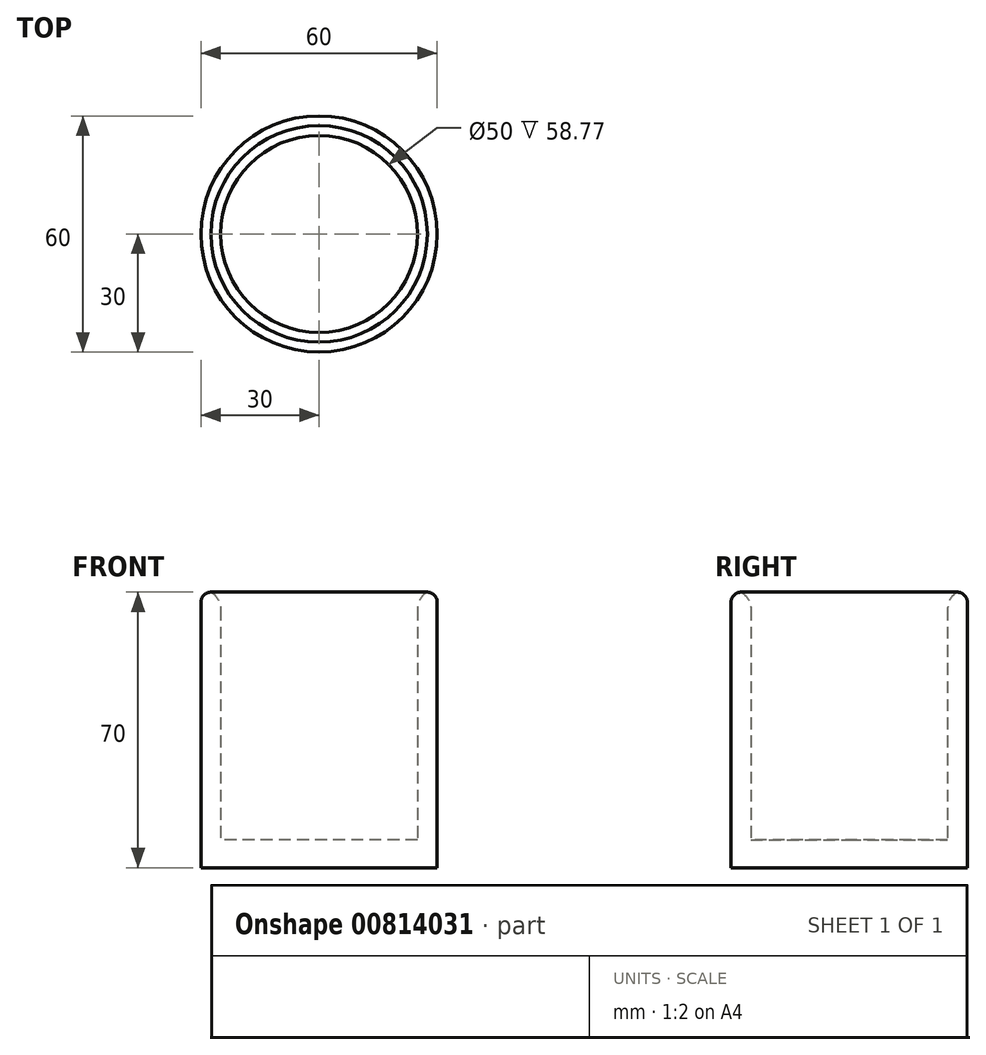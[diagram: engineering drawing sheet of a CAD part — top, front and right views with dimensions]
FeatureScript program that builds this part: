
annotation { "Feature Type Name" : "Feature", "Feature Type Description" : "" }
export const myFeature = defineFeature(function(context is Context, id is Id, definition is map)
    precondition{}
    {
        {
            var Q0;
            Q0=qCreatedBy(makeId("Top.planeOp"),FACE);
            var sketch = newSketch(context, id + "F0", { "sketchPlane" : qUnion([Q0])});
            skCircle(sketch, "E0", {"center": v(0, 0) * mm, "radius": 30 * mm});
            skCircle(sketch, "E1", {"center": v(0, 0) * mm, "radius": 25 * mm});
            skSolve(sketch);
        }
        {
            var Q0;
            Q0=makeQuery(id+"F0.imprint","IMPRINT",FACE,{"disambiguationData":[TD([[makeQuery(id+"F0.imprint","IMPRINT",EDGE,{"derivedFrom":sQuery(id+"F0.wireOp",EDGE,"E0")}),1.0]])]});
            var Q1;
            Q1=sQuery(id+"F0.wireOp",EDGE,"E0");
            var Q2;
            Q2=sQuery(id+"F0.wireOp",EDGE,"E1");
            extrude(context, id + "F1", {"entities" : qUnion([Q0]), "surfaceEntities" : qUnion([Q1, Q2]), "depth" : 70 * mm, "offsetDistance" : 25 * mm});
        }
        {
            var Q0;
            Q0=makeQuery(id+"F0.imprint","IMPRINT",FACE,{"disambiguationData":[TD([[makeQuery(id+"F0.imprint","IMPRINT",EDGE,{"derivedFrom":sQuery(id+"F0.wireOp",EDGE,"E1")}),1.0]])]});
            extrude(context, id + "F2", {"entities" : qUnion([Q0]), "operationType" : NewBodyOperationType.ADD, "depth" : 7 * mm, "offsetDistance" : 25 * mm});
        }
        {
            var Q0;
            Q0=makeQuery(id+"F1.opExtrude","CAP_EDGE",EDGE,{"disambiguationData":[OSD([sQuery(id+"F0.wireOp",EDGE,"E0")])],"isStart":false});
            fillet(context, id + "F3", {"entities" : qUnion([Q0]), "radius" : 2.5 * mm, "tangentPropagation" : true, "allowEdgeOverflow" : false});
        }
        {
            var Q0;
            Q0=makeQuery(id+"F1.opExtrude","CAP_EDGE",EDGE,{"disambiguationData":[OSD([sQuery(id+"F0.wireOp",EDGE,"E1")])],"isStart":false});
            fillet(context, id + "F4", {"entities" : qUnion([Q0]), "radius" : 4.83 * mm, "tangentPropagation" : true, "allowEdgeOverflow" : false});
        }
    });
